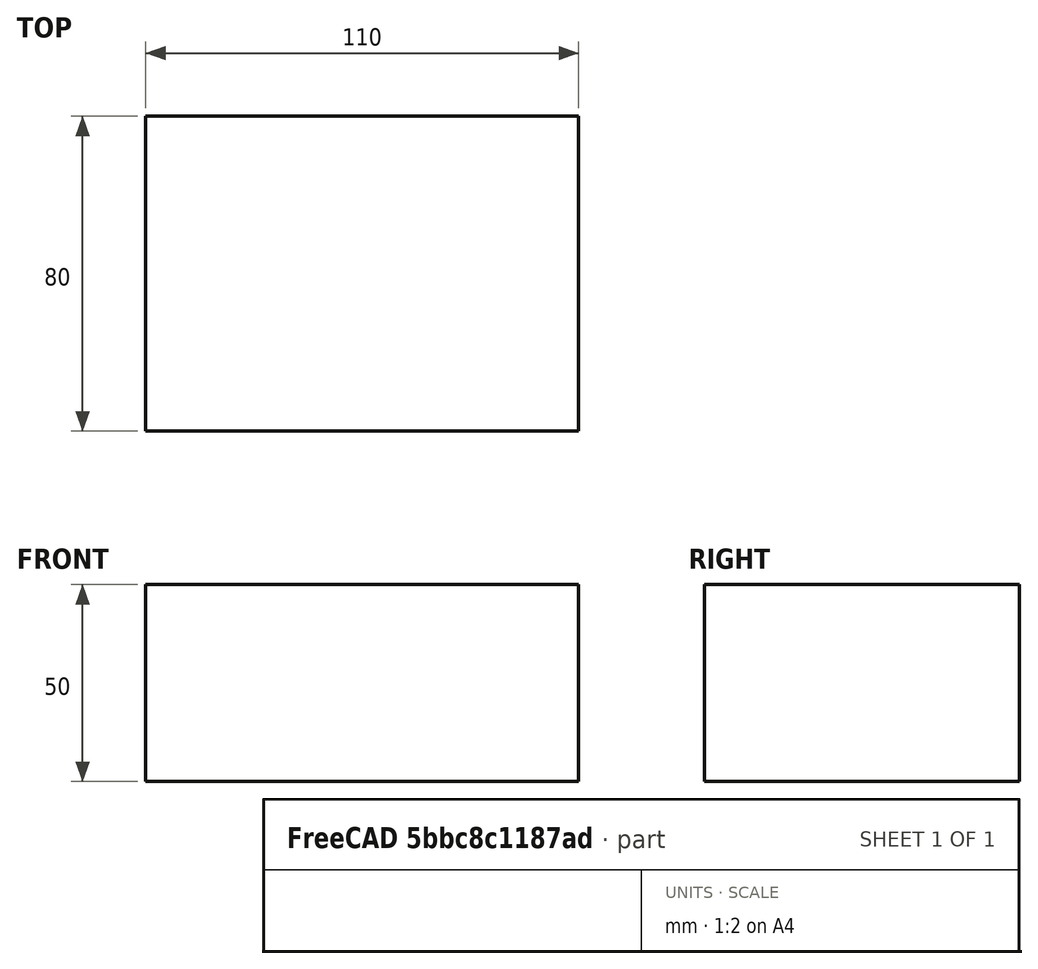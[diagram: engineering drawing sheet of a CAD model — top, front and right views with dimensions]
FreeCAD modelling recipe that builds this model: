
FCSTD DOCUMENT  (FreeCAD 0.18R16146 (Git))
Label: virtual_wall_fc-paso 2
License: All rights reserved
LicenseURL: http://en.wikipedia.org/wiki/All_rights_reserved
objects: Sketcher::SketchObject×2, PartDesign::Pad×1, PartDesign::Body×1
note: 5 computed .brp shape members not serialized (recipe doc carries the construction recipe); baked Part::Feature solids carry a one-line shape summary decoded from their .brp

FEATURE [Sketcher::SketchObject] Sketch
  MapMode = 5
  Support = -> [XY_Plane]
  sketch-geometry (4):
    g0: LineSegment StartX=0 StartY=0 StartZ=0 EndX=110 EndY=0 EndZ=0
    g1: LineSegment StartX=110 StartY=0 StartZ=0 EndX=110 EndY=80 EndZ=0
    g2: LineSegment StartX=110 StartY=80 StartZ=0 EndX=0 EndY=80 EndZ=0
    g3: LineSegment StartX=0 StartY=80 StartZ=0 EndX=0 EndY=0 EndZ=0
  constraints (11):
    c: Coincident(g0,g1)
    c: Coincident(g1,g2)
    c: Coincident(g2,g3)
    c: Coincident(g3,g0)
    c: Horizontal(g0)
    c: Horizontal(g2)
    c: Vertical(g1)
    c: Vertical(g3)
    c: Coincident(g0,g-1)
    c: DistanceX(g2,g2) = 110
    c: DistanceY(g1,g1) = 80
FEATURE [PartDesign::Pad] Pad
  Length = 50
  Length2 = 100
  Profile = -> Sketch
  Type = 0
FEATURE [Sketcher::SketchObject] Sketch001
  MapMode = 5
  Placement = pos=(0,0,50) rot=(0,0,1;0rad)
  Support = -> [Pad]
  sketch-geometry (13):
    g0: LineSegment StartX=2 StartY=10 StartZ=0 EndX=10 EndY=10 EndZ=0
    g1: LineSegment StartX=10 StartY=10 StartZ=0 EndX=10 EndY=2 EndZ=0
    g2: LineSegment StartX=10 StartY=2 StartZ=0 EndX=100 EndY=2 EndZ=0
    g3: LineSegment StartX=100 StartY=2 StartZ=0 EndX=100 EndY=10 EndZ=0
    g4: LineSegment StartX=100 StartY=10 StartZ=0 EndX=108 EndY=10 EndZ=0
    g5: LineSegment StartX=108 StartY=10 StartZ=0 EndX=108 EndY=70 EndZ=0
    g6: LineSegment StartX=108 StartY=70 StartZ=0 EndX=100 EndY=70 EndZ=0
    g7: LineSegment StartX=100 StartY=70 StartZ=0 EndX=100 EndY=78 EndZ=0
    g8: LineSegment StartX=100 StartY=78 StartZ=0 EndX=10 EndY=78 EndZ=0
    g9: LineSegment StartX=10 StartY=78 StartZ=0 EndX=10 EndY=70 EndZ=0
    g10: LineSegment StartX=10 StartY=70 StartZ=0 EndX=2 EndY=70 EndZ=0
    g11: LineSegment StartX=2 StartY=70 StartZ=0 EndX=2 EndY=10 EndZ=0
    g12: GeomPoint X=0 Y=0 Z=0
  constraints (37):
    c: Horizontal(g0)
    c: Coincident(g0,g1)
    c: Vertical(g1)
    c: Coincident(g1,g2)
    c: Horizontal(g2)
    c: Coincident(g2,g3)
    c: Coincident(g3,g4)
    c: Horizontal(g4)
    c: Coincident(g4,g5)
    c: Vertical(g5)
    c: Coincident(g5,g6)
    c: Horizontal(g6)
    c: Coincident(g6,g7)
    c: Coincident(g7,g8)
    c: Horizontal(g8)
    c: Coincident(g8,g9)
    c: Coincident(g9,g10)
    c: Coincident(g10,g11)
    c: Coincident(g11,g0)
    c: Vertical(g11)
    c: Vertical(g9)
    c: Vertical(g7)
    c: Vertical(g3)
    c: Horizontal(g10)
    c: DistanceX(g-1,g0) = 2
    c: DistanceY(g-1,g1) = 2
    c: DistanceX(g0,g0) = 8
    c: DistanceY(g1,g1) = 8
    c: DistanceX(g10,g10) = 8
    c: DistanceY(g9,g9) = 8
    c: Coincident(g12,g-1)
    c: DistanceY(g11,g11) = 60
    c: DistanceX(g8,g7) = 90
    c: DistanceY(g7,g7) = 8
    c: DistanceX(g6,g6) = 8
    c: DistanceY(g5,g5) = 60
    c: DistanceX(g4,g4) = 8
FEATURE [PartDesign::Body] Body
  Group = -> [Sketch,Pad,Sketch001]
  Origin = -> Origin
  Tip = -> Pad
